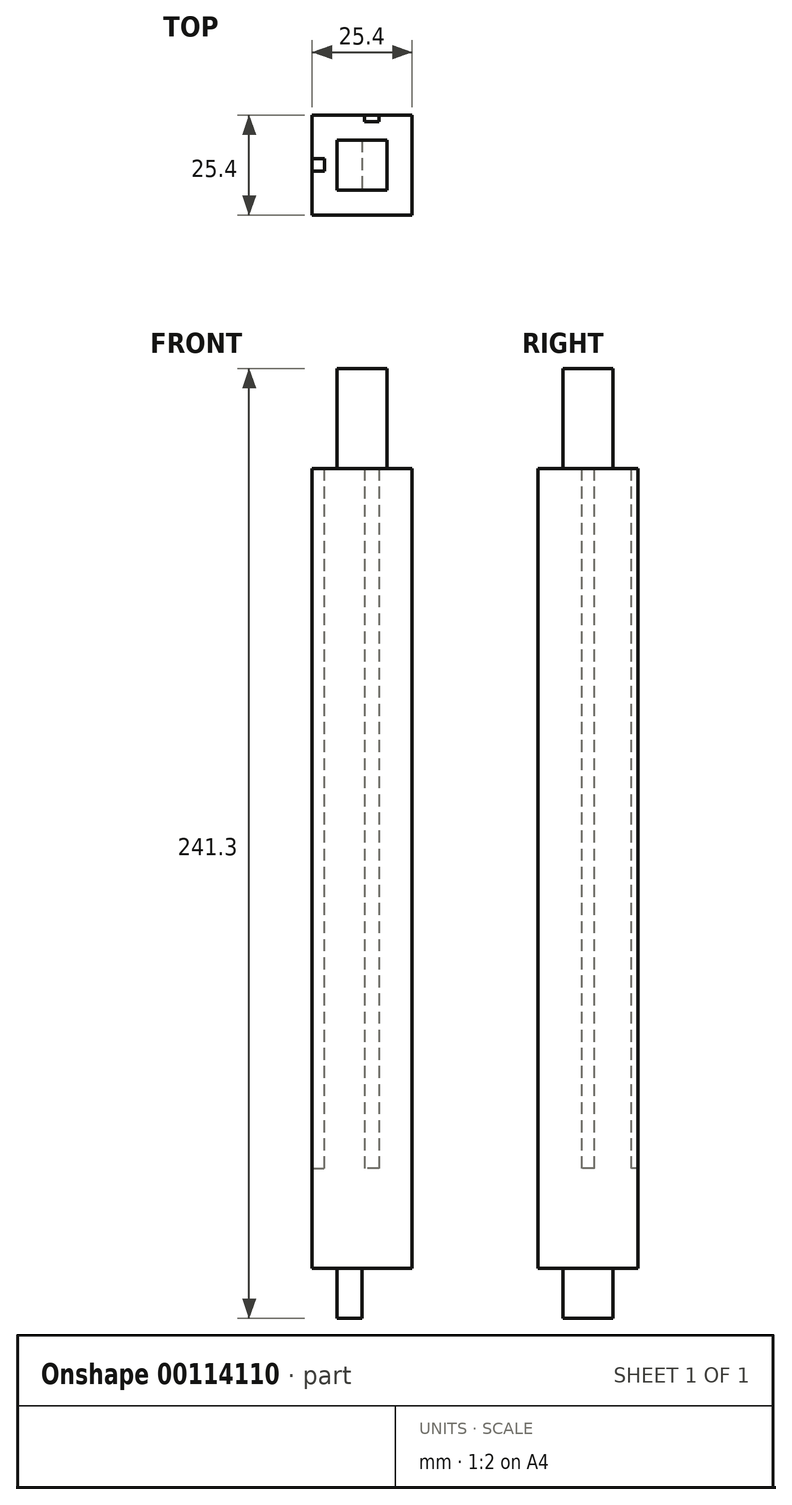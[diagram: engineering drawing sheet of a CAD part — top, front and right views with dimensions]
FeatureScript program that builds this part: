
annotation { "Feature Type Name" : "Feature", "Feature Type Description" : "" }
export const myFeature = defineFeature(function(context is Context, id is Id, definition is map)
    precondition{}
    {
        {
            var Q0;
            Q0=qCreatedBy(makeId("Top.planeOp"),FACE);
            var sketch = newSketch(context, id + "F0", { "sketchPlane" : qUnion([Q0])});
            skLineSegment(sketch, "E0.bottom", {"start": v(12.7, 12.7) * mm, "end": v(-12.7, 12.7) * mm});
            skLineSegment(sketch, "E0.top", {"start": v(12.7, -12.7) * mm, "end": v(-12.7, -12.7) * mm});
            skLineSegment(sketch, "E0.left", {"start": v(12.7, 12.7) * mm, "end": v(12.7, -12.7) * mm});
            skLineSegment(sketch, "E0.right", {"start": v(-12.7, 12.7) * mm, "end": v(-12.7, -12.7) * mm});
            skPoint(sketch, "E0.middle", {"position": v(0, 0) * mm});
            skSolve(sketch);
        }
        {
            var Q0;
            Q0 = qSketchRegion(id + "F0", true);
            extrude(context, id + "F1", {"entities" : qUnion([Q0]), "depth" : 203.2 * mm});
        }
        {
            var Q0;
            Q0=makeQuery(id+"F1.opExtrude","CAP_FACE",FACE,{"disambiguationData":[OSD([sQuery(id+"F0.wireOp",EDGE,"E0.bottom"),sQuery(id+"F0.wireOp",EDGE,"E0.top"),sQuery(id+"F0.wireOp",EDGE,"E0.left"),sQuery(id+"F0.wireOp",EDGE,"E0.right")])],"isStart":true});
            var sketch = newSketch(context, id + "F2", { "sketchPlane" : qUnion([Q0])});
            skLineSegment(sketch, "E1.bottom", {"start": v(-6.35, 6.35) * mm, "end": v(6.35, 6.35) * mm});
            skLineSegment(sketch, "E1.top", {"start": v(-6.35, -6.35) * mm, "end": v(6.35, -6.35) * mm});
            skLineSegment(sketch, "E1.left", {"start": v(-6.35, 6.35) * mm, "end": v(-6.35, -6.35) * mm});
            skLineSegment(sketch, "E1.right", {"start": v(6.35, 6.35) * mm, "end": v(6.35, -6.35) * mm});
            skPoint(sketch, "E1.middle", {"position": v(0, 0) * mm});
            skSolve(sketch);
        }
        {
            var Q0;
            Q0 = qSketchRegion(id + "F2", true);
            extrude(context, id + "F3", {"entities" : qUnion([Q0]), "operationType" : NewBodyOperationType.ADD, "depth" : 12.7 * mm});
        }
        {
            var Q0;
            Q0=makeQuery(id+"F3.opExtrude","CAP_FACE",FACE,{"disambiguationData":[OSD([sQuery(id+"F2.wireOp",EDGE,"E1.bottom"),sQuery(id+"F2.wireOp",EDGE,"E1.top"),sQuery(id+"F2.wireOp",EDGE,"E1.left"),sQuery(id+"F2.wireOp",EDGE,"E1.right")])],"isStart":false});
            var sketch = newSketch(context, id + "F4", { "sketchPlane" : qUnion([Q0])});
            skLineSegment(sketch, "E2.bottom", {"start": v(6.35, -6.35) * mm, "end": v(0, -6.35) * mm});
            skLineSegment(sketch, "E2.top", {"start": v(6.35, 6.35) * mm, "end": v(0, 6.35) * mm});
            skLineSegment(sketch, "E2.left", {"start": v(6.35, -6.35) * mm, "end": v(6.35, 6.35) * mm});
            skLineSegment(sketch, "E2.right", {"start": v(0, -6.35) * mm, "end": v(0, 6.35) * mm});
            skSolve(sketch);
        }
        {
            var Q0;
            Q0 = qSketchRegion(id + "F4", true);
            extrude(context, id + "F5", {"entities" : qUnion([Q0]), "operationType" : NewBodyOperationType.REMOVE, "oppositeDirection" : true, "depth" : 12.7 * mm});
        }
        {
            var Q0;
            Q0=makeQuery(id+"F1.opExtrude","CAP_FACE",FACE,{"disambiguationData":[OSD([sQuery(id+"F0.wireOp",EDGE,"E0.bottom"),sQuery(id+"F0.wireOp",EDGE,"E0.top"),sQuery(id+"F0.wireOp",EDGE,"E0.left"),sQuery(id+"F0.wireOp",EDGE,"E0.right")])],"isStart":false});
            var sketch = newSketch(context, id + "F6", { "sketchPlane" : qUnion([Q0])});
            skLineSegment(sketch, "E3.MirrorCS", {"start": v(4.3, 14.75) * mm, "end": v(4.3, 10.99) * mm});
            skLineSegment(sketch, "E4.MirrorCS", {"start": v(4.3, 10.99) * mm, "end": v(0.55, 10.99) * mm});
            skLineSegment(sketch, "E5.MirrorCS", {"start": v(0.55, 14.75) * mm, "end": v(0.55, 10.99) * mm});
            skLineSegment(sketch, "E6.MirrorCS", {"start": v(4.3, 14.75) * mm, "end": v(0.55, 14.75) * mm});
            skLineSegment(sketch, "E7.bottom", {"start": v(-12.7, 1.59) * mm, "end": v(-9.53, 1.59) * mm});
            skLineSegment(sketch, "E7.top", {"start": v(-12.7, -1.59) * mm, "end": v(-9.53, -1.59) * mm});
            skLineSegment(sketch, "E7.left", {"start": v(-12.7, 1.59) * mm, "end": v(-12.7, -1.59) * mm});
            skLineSegment(sketch, "E7.right", {"start": v(-9.53, 1.59) * mm, "end": v(-9.53, -1.59) * mm});
            skSolve(sketch);
        }
        {
            var Q0;
            Q0 = qSketchRegion(id + "F6", true);
            extrude(context, id + "F7", {"entities" : qUnion([Q0]), "operationType" : NewBodyOperationType.REMOVE, "oppositeDirection" : true, "depth" : 177.8 * mm});
        }
        {
            var Q0;
            Q0=makeQuery(id+"F1.opExtrude","CAP_FACE",FACE,{"disambiguationData":[OSD([sQuery(id+"F0.wireOp",EDGE,"E0.bottom"),sQuery(id+"F0.wireOp",EDGE,"E0.top"),sQuery(id+"F0.wireOp",EDGE,"E0.left"),sQuery(id+"F0.wireOp",EDGE,"E0.right")])],"isStart":false});
            var sketch = newSketch(context, id + "F8", { "sketchPlane" : qUnion([Q0])});
            skLineSegment(sketch, "E8.bottom", {"start": v(-6.35, 6.35) * mm, "end": v(6.35, 6.35) * mm});
            skLineSegment(sketch, "E8.top", {"start": v(-6.35, -6.35) * mm, "end": v(6.35, -6.35) * mm});
            skLineSegment(sketch, "E8.left", {"start": v(-6.35, 6.35) * mm, "end": v(-6.35, -6.35) * mm});
            skLineSegment(sketch, "E8.right", {"start": v(6.35, 6.35) * mm, "end": v(6.35, -6.35) * mm});
            skPoint(sketch, "E8.middle", {"position": v(0, 0) * mm});
            skSolve(sketch);
        }
        {
            var Q0;
            Q0 = qSketchRegion(id + "F8", true);
            extrude(context, id + "F9", {"entities" : qUnion([Q0]), "operationType" : NewBodyOperationType.ADD, "depth" : 25.4 * mm});
        }
    });
